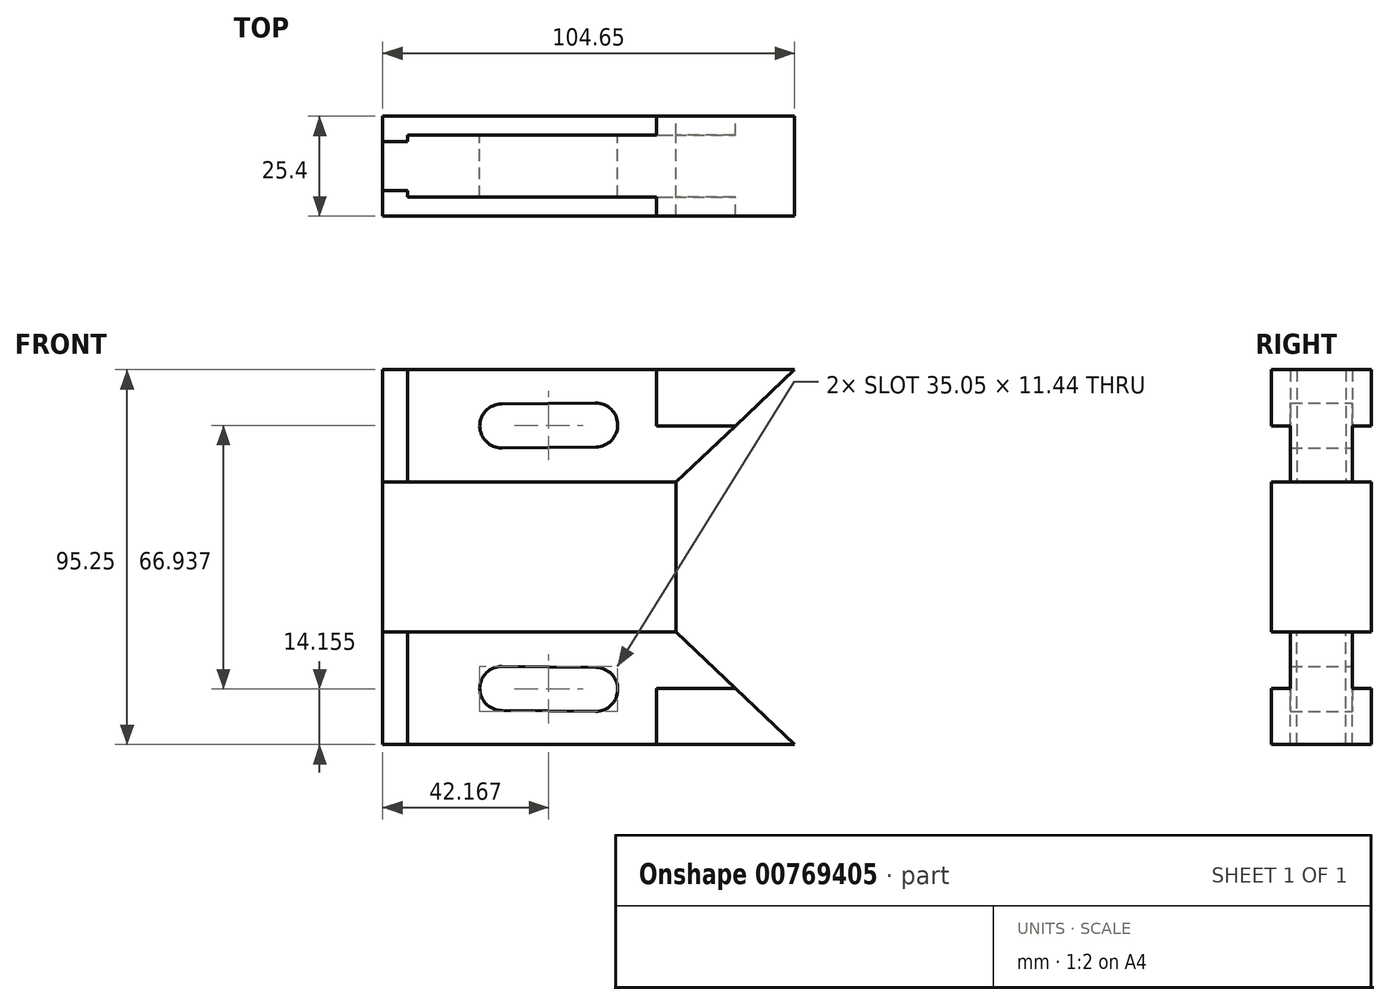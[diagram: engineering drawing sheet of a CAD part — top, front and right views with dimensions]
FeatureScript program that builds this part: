
annotation { "Feature Type Name" : "Feature", "Feature Type Description" : "" }
export const myFeature = defineFeature(function(context is Context, id is Id, definition is map)
    precondition{}
    {
        {
            var Q0;
            Q0=qCreatedBy(makeId("Front.planeOp"),FACE);
            var sketch = newSketch(context, id + "F0", { "sketchPlane" : qUnion([Q0])});
            skLineSegment(sketch, "E0.bottom", {"start": v(-42.12, 26.9) * mm, "end": v(62.53, 26.9) * mm});
            skLineSegment(sketch, "E0.top", {"start": v(-42.12, -1.67) * mm, "end": v(62.53, -1.67) * mm});
            skLineSegment(sketch, "E0.left", {"start": v(-42.12, 26.9) * mm, "end": v(-42.12, -1.67) * mm});
            skLineSegment(sketch, "E0.right", {"start": v(62.53, 26.9) * mm, "end": v(62.53, -1.67) * mm});
            skLineSegment(sketch, "E1.bottom", {"start": v(-42.12, -1.67) * mm, "end": v(32.36, -1.67) * mm});
            skLineSegment(sketch, "E1.top", {"start": v(-42.12, -20.72) * mm, "end": v(32.36, -20.72) * mm});
            skLineSegment(sketch, "E1.left", {"start": v(-42.12, -1.67) * mm, "end": v(-42.12, -20.72) * mm});
            skLineSegment(sketch, "E1.right", {"start": v(32.36, -1.67) * mm, "end": v(32.36, -20.72) * mm});
            skLineSegment(sketch, "E2", {"start": v(-35.77, 26.9) * mm, "end": v(-35.77, -1.67) * mm});
            skLineSegment(sketch, "E3", {"start": v(-42.12, 12.62) * mm, "end": v(62.53, 12.62) * mm, "construction": true});
            skLineSegment(sketch, "E4", {"start": v(62.53, 26.9) * mm, "end": v(32.36, -1.67) * mm});
            skLineSegment(sketch, "E5", {"start": v(-42.12, 4.68) * mm, "end": v(62.53, 4.68) * mm});
            skPoint(sketch, "E6.endSnap0", {"position": v(-35.77, 12.62) * mm});
            skCircle(sketch, "E7", {"center": v(-11.89, 12.62) * mm, "radius": 5.59 * mm});
            skCircle(sketch, "E8", {"center": v(11.98, 12.88) * mm, "radius": 5.59 * mm});
            skLineSegment(sketch, "E9", {"start": v(-11.95, 18.2) * mm, "end": v(11.92, 18.47) * mm});
            skLineSegment(sketch, "E10", {"start": v(-11.83, 7.03) * mm, "end": v(12.05, 7.3) * mm});
            skLineSegment(sketch, "E11", {"start": v(27.48, 26.9) * mm, "end": v(27.48, 12.62) * mm});
            skLineSegment(sketch, "E12", {"start": v(27.48, 12.62) * mm, "end": v(47.45, 12.62) * mm});
            skSolve(sketch);
        }
        {
            var Q0;
            {var subQ3=sQuery(id+"F0.wireOp",EDGE,"E11");Q0=makeQuery(id+"F0.imprint","IMPRINT",FACE,{"disambiguationData":[TD([[makeQuery(id+"F0.imprint","IMPRINT",EDGE,{"derivedFrom":subQ3}),1.0]])]});}
            var Q1;
            Q1=makeQuery(id+"F0.imprint","IMPRINT",FACE,{"disambiguationData":[TD([[makeQuery(id+"F0.imprint","IMPRINT",EDGE,{"derivedFrom":sQuery(id+"F0.wireOp",EDGE,"E1.top")}),1.0]])]});
            extrude(context, id + "F1", {"entities" : qUnion([Q0, Q1]), "endBound" : BoundingType.SYMMETRIC, "depth" : 25.4 * mm, "offsetDistance" : 25.4 * mm});
        }
        {
            var Q0;
            {var subQ7=sQuery(id+"F0.wireOp",EDGE,"E9");Q0=makeQuery(id+"F0.imprint","IMPRINT",FACE,{"disambiguationData":[TD([[makeQuery(id+"F0.imprint","IMPRINT",EDGE,{"derivedFrom":subQ7}),1.0]])]});}
            var Q1;
            {var subQ1=sQuery(id+"F0.wireOp",EDGE,"E1.bottom");var subQ3=sQuery(id+"F0.wireOp",EDGE,"E2");var subQ4=makeQuery(id+"F0.imprint","INTERSECT",VERTEX,{"derivedFrom":[subQ1,subQ3]});Q1=makeQuery(id+"F0.imprint","IMPRINT",FACE,{"disambiguationData":[TD([[makeQuery(id+"F0.imprint","IMPRINT",EDGE,{"disambiguationData":[TD([[subQ4,1.0]])],"derivedFrom":subQ3}),1.0]])]});}
            extrude(context, id + "F2", {"entities" : qUnion([Q0, Q1]), "operationType" : NewBodyOperationType.ADD, "endBound" : BoundingType.SYMMETRIC, "depth" : 15.75 * mm, "offsetDistance" : 25.4 * mm});
        }
        {
            var Q0;
            {var subQ0=sQuery(id+"F0.wireOp",EDGE,"E0.left");var subQ1=sQuery(id+"F0.wireOp",EDGE,"E0.bottom");var subQ2=makeQuery(id+"F0.imprint","INTERSECT",VERTEX,{"derivedFrom":[subQ1,subQ0]});Q0=makeQuery(id+"F0.imprint","IMPRINT",FACE,{"disambiguationData":[TD([[makeQuery(id+"F0.imprint","IMPRINT",EDGE,{"disambiguationData":[TD([[subQ2,-1.0]])],"derivedFrom":subQ1}),-1.0]])]});}
            var Q1;
            {var subQ0=sQuery(id+"F0.wireOp",EDGE,"E1.bottom");var subQ5=sQuery(id+"F0.wireOp",EDGE,"E2");var subQ6=makeQuery(id+"F0.imprint","INTERSECT",VERTEX,{"derivedFrom":[subQ0,subQ5]});Q1=makeQuery(id+"F0.imprint","IMPRINT",FACE,{"disambiguationData":[TD([[makeQuery(id+"F0.imprint","IMPRINT",EDGE,{"disambiguationData":[TD([[subQ6,1.0]])],"derivedFrom":subQ5}),-1.0]])]});}
            extrude(context, id + "F3", {"entities" : qUnion([Q0, Q1]), "endBound" : BoundingType.SYMMETRIC, "depth" : 12.45 * mm, "offsetDistance" : 25 * mm});
        }
        {
            var Q0;
            Q0=makeQuery(id+"F1.opExtrude","SWEPT_BODY",BODY,{"disambiguationData":[OSD([sQuery(id+"F0.wireOp",EDGE,"E0.bottom"),sQuery(id+"F0.wireOp",EDGE,"E4"),sQuery(id+"F0.wireOp",EDGE,"E11"),sQuery(id+"F0.wireOp",EDGE,"E12")])]});
            var Q1;
            Q1=makeQuery(id+"F1.opExtrude","SWEPT_BODY",BODY,{"disambiguationData":[OSD([sQuery(id+"F0.wireOp",EDGE,"E1.bottom"),sQuery(id+"F0.wireOp",EDGE,"E1.top"),sQuery(id+"F0.wireOp",EDGE,"E1.left"),sQuery(id+"F0.wireOp",EDGE,"E1.right")])]});
            var Q2;
            Q2=makeQuery(id+"F3.opExtrude","SWEPT_BODY",BODY,{"disambiguationData":[OSD([sQuery(id+"F0.wireOp",EDGE,"E0.bottom"),sQuery(id+"F0.wireOp",EDGE,"E0.left"),sQuery(id+"F0.wireOp",EDGE,"E1.bottom"),sQuery(id+"F0.wireOp",EDGE,"E2")])]});
            var Q3;
            Q3=makeQuery(id+"F1.opExtrude","SWEPT_FACE",FACE,{"disambiguationData":[OSD([sQuery(id+"F0.wireOp",EDGE,"E1.top")])]});
            mirror(context, id + "F4", {"operationType" : NewBodyOperationType.ADD, "entities" : qUnion([Q0, Q1, Q2]), "mirrorPlane" : qUnion([Q3])});
        }
    });
